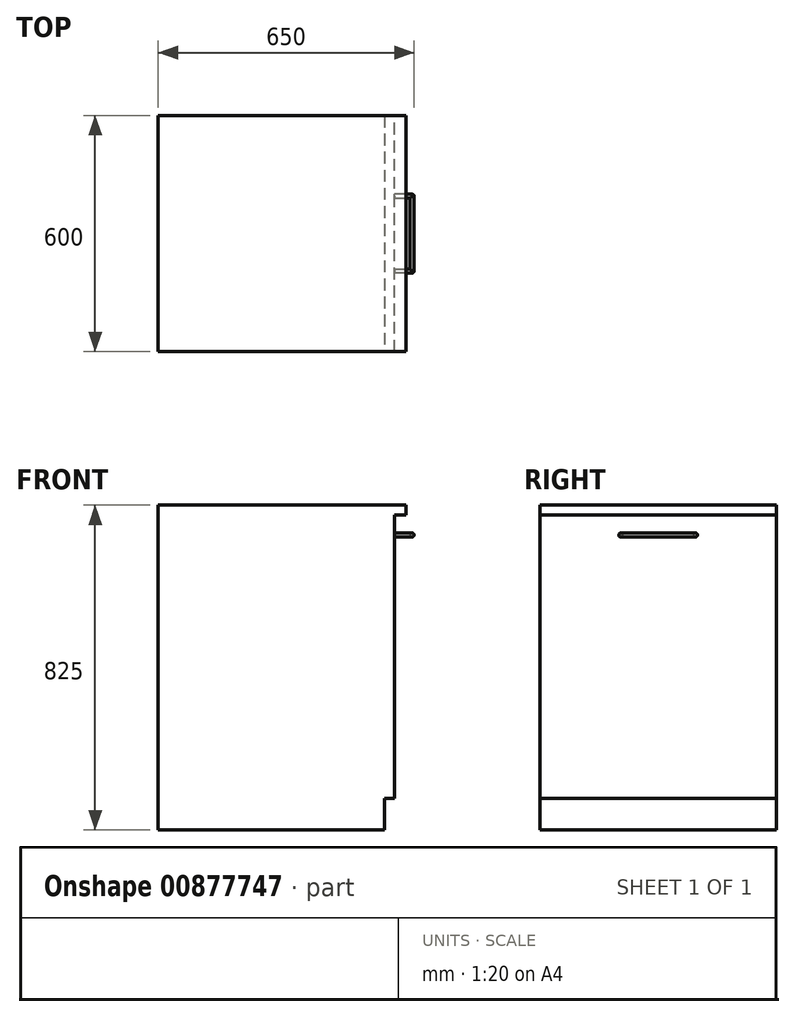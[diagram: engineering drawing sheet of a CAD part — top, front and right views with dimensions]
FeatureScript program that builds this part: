
annotation { "Feature Type Name" : "Feature", "Feature Type Description" : "" }
export const myFeature = defineFeature(function(context is Context, id is Id, definition is map)
    precondition{}
    {
        {
            var Q0;
            Q0=qCreatedBy(makeId("Top.planeOp"),FACE);
            var sketch = newSketch(context, id + "F0", { "sketchPlane" : qUnion([Q0])});
            skLineSegment(sketch, "E0.bottom", {"start": v(-300, 300) * mm, "end": v(300, 300) * mm});
            skLineSegment(sketch, "E0.top", {"start": v(-300, -300) * mm, "end": v(300, -300) * mm});
            skLineSegment(sketch, "E0.left", {"start": v(-300, 300) * mm, "end": v(-300, -300) * mm});
            skLineSegment(sketch, "E0.right", {"start": v(300, 300) * mm, "end": v(300, -300) * mm});
            skPoint(sketch, "E0.middle", {"position": v(0, 0) * mm});
            skSolve(sketch);
        }
        {
            var Q0;
            Q0=qSketchRegion(id+"F0",true);
            extrude(context, id + "F1", {"entities" : qUnion([Q0]), "depth" : 800 * mm, "offsetDistance" : 25 * mm});
        }
        {
            var Q0;
            Q0=makeQuery(id+"F1.opExtrude","SWEPT_FACE",FACE,{"disambiguationData":[OSD([sQuery(id+"F0.wireOp",EDGE,"E0.right")])]});
            var sketch = newSketch(context, id + "F2", { "sketchPlane" : qUnion([Q0])});
            skLineSegment(sketch, "E1.bottom", {"start": v(-300, 0) * mm, "end": v(300, 0) * mm});
            skLineSegment(sketch, "E1.top", {"start": v(-300, 80) * mm, "end": v(300, 80) * mm});
            skLineSegment(sketch, "E1.left", {"start": v(-300, 0) * mm, "end": v(-300, 80) * mm});
            skLineSegment(sketch, "E1.right", {"start": v(300, 0) * mm, "end": v(300, 80) * mm});
            skSolve(sketch);
        }
        {
            var Q0;
            Q0=qSketchRegion(id+"F2",true);
            extrude(context, id + "F3", {"entities" : qUnion([Q0]), "operationType" : NewBodyOperationType.REMOVE, "oppositeDirection" : true, "depth" : 25 * mm, "offsetDistance" : 25 * mm});
        }
        {
            var Q0;
            Q0=makeQuery(id+"F1.opExtrude","CAP_FACE",FACE,{"disambiguationData":[OSD([sQuery(id+"F0.wireOp",EDGE,"E0.bottom"),sQuery(id+"F0.wireOp",EDGE,"E0.top"),sQuery(id+"F0.wireOp",EDGE,"E0.left"),sQuery(id+"F0.wireOp",EDGE,"E0.right")])],"isStart":false});
            var sketch = newSketch(context, id + "F4", { "sketchPlane" : qUnion([Q0])});
            skLineSegment(sketch, "E2.bottom", {"start": v(-300, -300) * mm, "end": v(330, -300) * mm});
            skLineSegment(sketch, "E2.top", {"start": v(-300, 300) * mm, "end": v(330, 300) * mm});
            skLineSegment(sketch, "E2.left", {"start": v(-300, -300) * mm, "end": v(-300, 300) * mm});
            skLineSegment(sketch, "E2.right", {"start": v(330, -300) * mm, "end": v(330, 300) * mm});
            skSolve(sketch);
        }
        {
            var Q0;
            Q0=qSketchRegion(id+"F4",true);
            extrude(context, id + "F5", {"entities" : qUnion([Q0]), "operationType" : NewBodyOperationType.ADD, "depth" : 25 * mm, "offsetDistance" : 25 * mm});
        }
        {
            var Q0;
            Q0=makeQuery(id+"F1.opExtrude","SWEPT_FACE",FACE,{"disambiguationData":[OSD([sQuery(id+"F0.wireOp",EDGE,"E0.right")])]});
            var sketch = newSketch(context, id + "F6", { "sketchPlane" : qUnion([Q0])});
            skLineSegment(sketch, "E3.bottom", {"start": v(95, 754.24) * mm, "end": v(-95, 754.24) * mm});
            skLineSegment(sketch, "E3.top", {"start": v(95, 744.24) * mm, "end": v(-95, 744.24) * mm});
            skLineSegment(sketch, "E3.left", {"start": v(100, 749.24) * mm, "end": v(100, 749.24) * mm});
            skLineSegment(sketch, "E3.right", {"start": v(-100, 749.24) * mm, "end": v(-100, 749.24) * mm});
            skPoint(sketch, "E3.middle", {"position": v(0, 749.24) * mm});
            skPoint(sketch, "E3.middle.positionSnap0", {"position": v(0, 80) * mm});
            skPoint(sketch, "E3.centerSnap0", {"position": v(0, 80) * mm});
            skPoint(sketch, "E4.visualSharp", {"position": v(100, 744.24) * mm});
            skArc(sketch, "E4.filletArc", {"start": v(95, 744.24) * mm, "mid": v(98.54, 745.7) * mm, "end": v(100, 749.24) * mm});
            skPoint(sketch, "E5.visualSharp", {"position": v(100, 754.24) * mm});
            skArc(sketch, "E5.filletArc", {"start": v(100, 749.24) * mm, "mid": v(98.54, 752.78) * mm, "end": v(95, 754.24) * mm});
            skPoint(sketch, "E6.visualSharp", {"position": v(-100, 754.24) * mm});
            skArc(sketch, "E6.filletArc", {"start": v(-95, 754.24) * mm, "mid": v(-98.54, 752.78) * mm, "end": v(-100, 749.24) * mm});
            skPoint(sketch, "E7.visualSharp", {"position": v(-100, 744.24) * mm});
            skArc(sketch, "E7.filletArc", {"start": v(-100, 749.24) * mm, "mid": v(-98.54, 745.7) * mm, "end": v(-95, 744.24) * mm});
            skSolve(sketch);
        }
        {
            var Q0;
            Q0=qSketchRegion(id+"F6",true);
            extrude(context, id + "F7", {"entities" : qUnion([Q0]), "operationType" : NewBodyOperationType.ADD, "depth" : 50 * mm, "offsetDistance" : 25 * mm});
        }
        {
            var Q0;
            Q0=makeQuery(id+"F7.opExtrude","SWEPT_FACE",FACE,{"disambiguationData":[OSD([sQuery(id+"F6.wireOp",EDGE,"E3.top")])]});
            var sketch = newSketch(context, id + "F8", { "sketchPlane" : qUnion([Q0])});
            skLineSegment(sketch, "E8.bottom", {"start": v(300, 90) * mm, "end": v(340, 90) * mm});
            skLineSegment(sketch, "E8.top", {"start": v(300, -90) * mm, "end": v(340, -90) * mm});
            skLineSegment(sketch, "E8.left", {"start": v(300, 90) * mm, "end": v(300, -90) * mm});
            skLineSegment(sketch, "E8.right", {"start": v(340, 90) * mm, "end": v(340, -90) * mm});
            skSolve(sketch);
        }
        {
            var Q0;
            Q0=qSketchRegion(id+"F8",true);
            extrude(context, id + "F9", {"entities" : qUnion([Q0]), "operationType" : NewBodyOperationType.REMOVE, "oppositeDirection" : true, "depth" : 25 * mm, "offsetDistance" : 25 * mm});
        }
        {
            var Q0;
            Q0=makeQuery(id+"F7.opExtrude","CAP_EDGE",EDGE,{"disambiguationData":[OSD([sQuery(id+"F6.wireOp",EDGE,"E4.filletArc"),sQuery(id+"F6.wireOp",EDGE,"E5.filletArc")])],"isStart":false});
            var Q1;
            Q1=makeQuery(id+"F7.opExtrude","CAP_EDGE",EDGE,{"disambiguationData":[OSD([sQuery(id+"F6.wireOp",EDGE,"E3.bottom")])],"isStart":false});
            var Q2;
            Q2=makeQuery(id+"F7.opExtrude","CAP_EDGE",EDGE,{"disambiguationData":[OSD([sQuery(id+"F6.wireOp",EDGE,"E3.top")])],"isStart":false});
            var Q3;
            Q3=makeQuery(id+"F9.boolean.opBoolean","COPY",EDGE,{"derivedFrom":makeQuery(id+"F9.opExtrude","CAP_EDGE",EDGE,{"disambiguationData":[OSD([sQuery(id+"F8.wireOp",EDGE,"E8.top")])],"isStart":true})});
            var Q4;
            Q4=makeQuery(id+"F9.boolean.opBoolean","COPY",EDGE,{"derivedFrom":makeQuery(id+"F9.opExtrude","CAP_EDGE",EDGE,{"disambiguationData":[OSD([sQuery(id+"F8.wireOp",EDGE,"E8.right")])],"isStart":true})});
            var Q5;
            Q5=makeQuery(id+"F9.boolean.opBoolean","COPY",EDGE,{"derivedFrom":makeQuery(id+"F9.opExtrude","CAP_EDGE",EDGE,{"disambiguationData":[OSD([sQuery(id+"F8.wireOp",EDGE,"E8.bottom")])],"isStart":true})});
            var Q6;
            Q6=makeQuery(id+"F9.boolean.opBoolean","INTERSECT",EDGE,{"derivedFrom":[makeQuery(id+"F7.opExtrude","SWEPT_FACE",FACE,{"disambiguationData":[OSD([sQuery(id+"F6.wireOp",EDGE,"E3.bottom")])]}),makeQuery(id+"F9.opExtrude","SWEPT_FACE",FACE,{"disambiguationData":[OSD([sQuery(id+"F8.wireOp",EDGE,"E8.top")])]})]});
            var Q7;
            Q7=makeQuery(id+"F9.boolean.opBoolean","INTERSECT",EDGE,{"derivedFrom":[makeQuery(id+"F7.opExtrude","SWEPT_FACE",FACE,{"disambiguationData":[OSD([sQuery(id+"F6.wireOp",EDGE,"E3.bottom")])]}),makeQuery(id+"F9.opExtrude","SWEPT_FACE",FACE,{"disambiguationData":[OSD([sQuery(id+"F8.wireOp",EDGE,"E8.right")])]})]});
            var Q8;
            Q8=makeQuery(id+"F9.boolean.opBoolean","INTERSECT",EDGE,{"derivedFrom":[makeQuery(id+"F7.opExtrude","SWEPT_FACE",FACE,{"disambiguationData":[OSD([sQuery(id+"F6.wireOp",EDGE,"E3.bottom")])]}),makeQuery(id+"F9.opExtrude","SWEPT_FACE",FACE,{"disambiguationData":[OSD([sQuery(id+"F8.wireOp",EDGE,"E8.bottom")])]})]});
            var Q9;
            Q9=makeQuery(id+"F7.opExtrude","CAP_EDGE",EDGE,{"disambiguationData":[OSD([sQuery(id+"F6.wireOp",EDGE,"E6.filletArc"),sQuery(id+"F6.wireOp",EDGE,"E7.filletArc")])],"isStart":false});
            fillet(context, id + "F10", {"entities" : qUnion([Q0, Q1, Q2, Q3, Q4, Q5, Q6, Q7, Q8, Q9]), "radius" : 5 * mm, "tangentPropagation" : true, "allowEdgeOverflow" : false});
        }
    });
